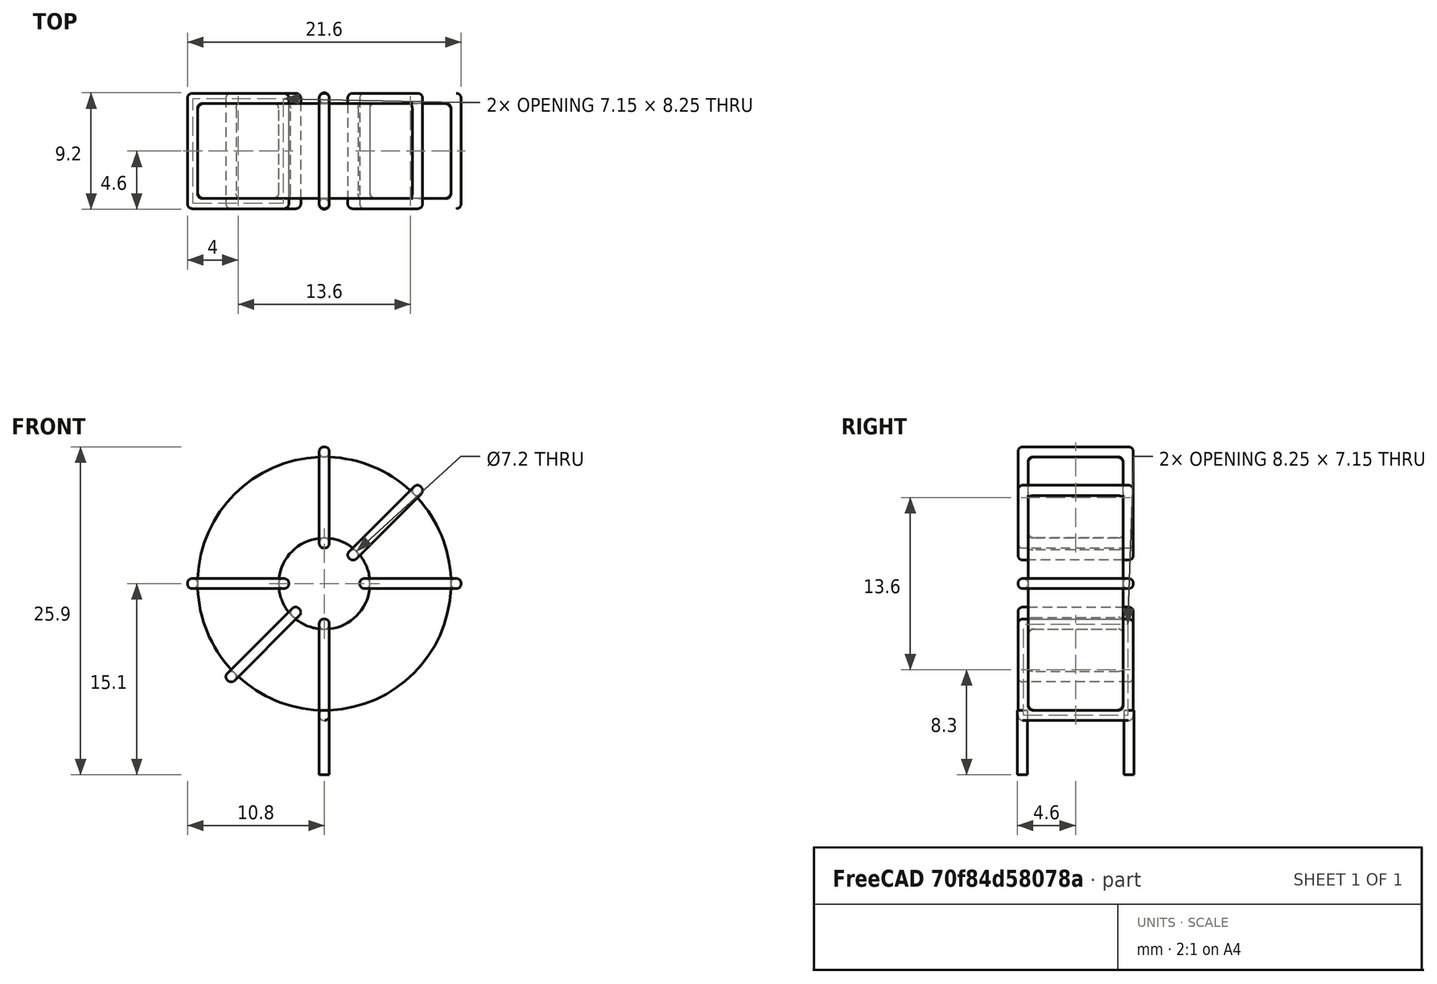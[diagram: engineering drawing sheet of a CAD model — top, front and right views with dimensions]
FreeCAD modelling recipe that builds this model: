
FCSTD DOCUMENT  (FreeCAD 0.16R6703 (Git))
Label: L_Toroid_Vertical_L21.6mm_W9.1mm_P8.40mm_Bourns_5700series
License: All rights reserved
LicenseURL: http://en.wikipedia.org/wiki/All_rights_reserved
objects: Sketcher::SketchObject×6, PartDesign::Pad×6, PartDesign::Fillet×5, Spreadsheet::Sheet×1
note: 23 computed .brp shape members not serialized (recipe doc carries the construction recipe); baked Part::Feature solids carry a one-line shape summary decoded from their .brp

FEATURE [Spreadsheet::Sheet] Spreadsheet  label="dimensions"
  cells = A1=Wx; B1(Wx)=21.6; C1(WW)=7.2; D1=21.6; A2=Wy; B2(Wy)=9.1; D2=9.1; A3=RM; B3(RMx)=8.4; C3(RMy)=0; A4=d_wire; B4(d_wire)=0.8; A5=H; B5(H)=21.6; A6=offsetx; B6(offsetx)=10.8
FEATURE [Sketcher::SketchObject] Sketch
  Placement = pos=(0,-4.2,0) rot=(1,0,0;1.5708rad)
  expr: Placement.Base.y = -Spreadsheet.RMx / 2
  expr: Constraints[0] = Spreadsheet.Wx / 2 - Spreadsheet.d_wire
  expr: Constraints[4] = Spreadsheet.WW / 2
  expr: Constraints[2] = Spreadsheet.Wx / 2 + Spreadsheet.d_wire + 0.5
  sketch-geometry (2):
    g0: Circle CenterX=0 CenterY=12.1 CenterZ=0 NormalX=0 NormalY=0 NormalZ=1 Radius=10
    g1: Circle CenterX=0 CenterY=12.1 CenterZ=0 NormalX=0 NormalY=0 NormalZ=1 Radius=3.6
  constraints (5):
    c: Radius(g0) = 10
    c: DistanceX(g-1,g0) = 0
    c: DistanceY(g-1,g0) = 12.1
    c: Coincident(g1,g0)
    c: Radius(g1) = 3.6
FEATURE [PartDesign::Pad] Pad
  Length = 7.5
  Length2 = 100
  Midplane = true
  Placement = pos=(0,-4.2,0) rot=(1,0,0;1.5708rad)
  Sketch = -> Sketch
  Type = 0
  expr: Length = Spreadsheet.Wy - 2 * Spreadsheet.d_wire
FEATURE [Sketcher::SketchObject] Sketch001
  Placement = pos=(0,0,1.3) rot=(0,0,1;0rad)
  expr: Placement.Base.z = 0.5 + Spreadsheet.d_wire
  expr: Constraints[4] = Spreadsheet.RMy
  expr: Constraints[2] = -Spreadsheet.RMx
  expr: Constraints[1] = Spreadsheet.d_wire / 2
  sketch-geometry (2):
    g0: Circle CenterX=0 CenterY=0 CenterZ=0 NormalX=0 NormalY=0 NormalZ=1 Radius=0.4
    g1: Circle CenterX=0 CenterY=-8.4 CenterZ=0 NormalX=0 NormalY=0 NormalZ=1 Radius=0.4
  constraints (5):
    c: Equal(g0,g1)
    c: Radius(g0) = 0.4
    c: DistanceY(g-1,g1) = -8.4
    c: Coincident(g0,g-1)
    c: DistanceX(g-1,g1) = 0
FEATURE [PartDesign::Pad] Pad001
  Length = 0.8
  Length2 = 4.3
  Placement = pos=(0,0,1.3) rot=(0,0,1;0rad)
  Reversed = true
  Sketch = -> Sketch001
  Type = 4
  expr: Length2 = 3.5 + Spreadsheet.d_wire
  expr: Length = Spreadsheet.d_wire
FEATURE [PartDesign::Fillet] Fillet
  Base = -> Pad [Edge6,Edge3,Edge2]
  Placement = pos=(0,-4.2,0) rot=(1,0,0;1.5708rad)
  Radius = 0.5
FEATURE [Sketcher::SketchObject] Sketch003
  Placement = pos=(0,0.35,12.1) rot=(1,0,0;3.14159rad)
  expr: Constraints[18] = Spreadsheet.d_wire
  expr: Constraints[16] = Spreadsheet.d_wire
  expr: Constraints[19] = Spreadsheet.d_wire
  expr: Constraints[17] = Spreadsheet.d_wire
  expr: Placement.Base.y = -1 * (Spreadsheet.RMx - Spreadsheet.Wy) / 2
  expr: Constraints[21] = (Spreadsheet.Wx - Spreadsheet.WW) / 2 - Spreadsheet.d_wire
  expr: Constraints[22] = Spreadsheet.Wx / 2 - Spreadsheet.d_wire
  expr: Constraints[43] = Spreadsheet.d_wire
  expr: Constraints[48] = Spreadsheet.Wx - Spreadsheet.d_wire * 2
  expr: Constraints[49] = Spreadsheet.Wy
  expr: Placement.Base.z = Spreadsheet.Wx / 2 + Spreadsheet.d_wire + 0.5
  sketch-geometry (16):
    g0: LineSegment StartX=-2.8 StartY=0 StartZ=0 EndX=-10.8 EndY=0 EndZ=0
    g1: LineSegment StartX=-10.8 StartY=0 StartZ=0 EndX=-10.8 EndY=9.1 EndZ=0
    g2: LineSegment StartX=-10.8 StartY=9.1 StartZ=0 EndX=-2.8 EndY=9.1 EndZ=0
    g3: LineSegment StartX=-2.8 StartY=9.1 StartZ=0 EndX=-2.8 EndY=0 EndZ=0
    g4: LineSegment StartX=-10 StartY=8.3 StartZ=0 EndX=-3.6 EndY=8.3 EndZ=0
    g5: LineSegment StartX=-3.6 StartY=8.3 StartZ=0 EndX=-3.6 EndY=0.8 EndZ=0
    g6: LineSegment StartX=-3.6 StartY=0.8 StartZ=0 EndX=-10 EndY=0.8 EndZ=0
    g7: LineSegment StartX=-10 StartY=0.8 StartZ=0 EndX=-10 EndY=8.3 EndZ=0
    g8: LineSegment StartX=2.8 StartY=9.1 StartZ=0 EndX=10.8 EndY=9.1 EndZ=0
    g9: LineSegment StartX=10.8 StartY=9.1 StartZ=0 EndX=10.8 EndY=0 EndZ=0
    g10: LineSegment StartX=10.8 StartY=0 StartZ=0 EndX=2.8 EndY=0 EndZ=0
    g11: LineSegment StartX=2.8 StartY=0 StartZ=0 EndX=2.8 EndY=9.1 EndZ=0
    g12: LineSegment StartX=3.6 StartY=8.3 StartZ=0 EndX=10 EndY=8.3 EndZ=0
    g13: LineSegment StartX=10 StartY=8.3 StartZ=0 EndX=10 EndY=0.8 EndZ=0
    g14: LineSegment StartX=10 StartY=0.8 StartZ=0 EndX=3.6 EndY=0.8 EndZ=0
    g15: LineSegment StartX=3.6 StartY=0.8 StartZ=0 EndX=3.6 EndY=8.3 EndZ=0
  constraints (50):
    c: Horizontal(g0)
    c: Coincident(g1,g0)
    c: Vertical(g1)
    c: Coincident(g2,g1)
    c: Horizontal(g2)
    c: Coincident(g3,g2)
    c: Coincident(g3,g0)
    c: Vertical(g3)
    c: Coincident(g4,g5)
    c: Coincident(g5,g6)
    c: Coincident(g6,g7)
    c: Coincident(g7,g4)
    c: Horizontal(g4)
    c: Horizontal(g6)
    c: Vertical(g5)
    c: Vertical(g7)
    c: DistanceX(g1,g4) = 0.8
    c: DistanceY(g4,g1) = 0.8
    c: DistanceX(g5,g0) = 0.8
    c: DistanceY(g0,g5) = 0.8
    c: DistanceY(g-1,g0) = 0
    c: DistanceX(g6,g6) = 6.4
    c: DistanceX(g6,g-1) = 10
    c: Coincident(g8,g9)
    c: Coincident(g9,g10)
    c: Coincident(g10,g11)
    c: Coincident(g11,g8)
    c: Horizontal(g8)
    c: Horizontal(g10)
    c: Vertical(g9)
    c: Vertical(g11)
    c: Coincident(g12,g13)
    c: Coincident(g13,g14)
    c: Coincident(g14,g15)
    c: Coincident(g15,g12)
    c: Horizontal(g12)
    c: Horizontal(g14)
    c: Vertical(g13)
    c: Vertical(g15)
    c: DistanceY(g8,g2) = 0
    c: DistanceY(g10,g0) = 0
    c: DistanceY(g14,g5) = 0
    c: DistanceY(g12,g4) = 0
    c: DistanceX(g8,g12) = 0.8
    c: Equal(g8,g2)
    c: Equal(g12,g4)
    c: Equal(g9,g1)
    c: Equal(g13,g7)
    c: DistanceX(g4,g12) = 20
    c: DistanceY(g0,g1) = 9.1
FEATURE [PartDesign::Pad] Pad002
  Length = 0.8
  Length2 = 100
  Midplane = true
  Placement = pos=(0,0.35,12.1) rot=(1,0,0;3.14159rad)
  Sketch = -> Sketch003
  Type = 0
  expr: Length = Spreadsheet.d_wire
FEATURE [PartDesign::Fillet] Fillet001
  Base = -> Pad002 [Edge38,Edge41,Edge42,Edge43,Edge29,Edge32,Edge33,Edge34,Edge25,Edge35,Edge36,Edge13,Edge14,Edge15,Edge16,Edge17,Edge18,Edge19,Edge1,Edge2,Edge3,Edge4,Edge5,Edge6,Edge7,Edge37,Edge39,Edge40,Edge20,Edge23,Edge24,Edge21,Edge22,Edge8,Edge9,Edge10,Edge11,Edge12,Edge26,Edge27,+8 more]
  Placement = pos=(0,0.35,12.1) rot=(1,0,0;3.14159rad)
  Radius = 0.376
  expr: Radius = Spreadsheet.d_wire * 0.47
FEATURE [Sketcher::SketchObject] Sketch004
  Placement = pos=(0,0.35,12.1) rot=(0.92388,0,0.382683;3.14159rad)
  expr: Constraints[18] = Spreadsheet.d_wire
  expr: Constraints[16] = Spreadsheet.d_wire
  expr: Constraints[19] = Spreadsheet.d_wire
  expr: Constraints[17] = Spreadsheet.d_wire
  expr: Placement.Base.y = -1 * (Spreadsheet.RMx - Spreadsheet.Wy) / 2
  expr: Constraints[21] = (Spreadsheet.Wx - Spreadsheet.WW) / 2 - Spreadsheet.d_wire
  expr: Constraints[22] = Spreadsheet.Wx / 2 - Spreadsheet.d_wire
  expr: Constraints[43] = Spreadsheet.d_wire
  expr: Constraints[48] = Spreadsheet.Wx - 2 * Spreadsheet.d_wire
  expr: Constraints[49] = Spreadsheet.Wy
  expr: Placement.Base.z = Spreadsheet.Wx / 2 + Spreadsheet.d_wire + 0.5
  sketch-geometry (16):
    g0: LineSegment StartX=-2.8 StartY=0 StartZ=0 EndX=-10.8 EndY=0 EndZ=0
    g1: LineSegment StartX=-10.8 StartY=0 StartZ=0 EndX=-10.8 EndY=9.1 EndZ=0
    g2: LineSegment StartX=-10.8 StartY=9.1 StartZ=0 EndX=-2.8 EndY=9.1 EndZ=0
    g3: LineSegment StartX=-2.8 StartY=9.1 StartZ=0 EndX=-2.8 EndY=0 EndZ=0
    g4: LineSegment StartX=-10 StartY=8.3 StartZ=0 EndX=-3.6 EndY=8.3 EndZ=0
    g5: LineSegment StartX=-3.6 StartY=8.3 StartZ=0 EndX=-3.6 EndY=0.8 EndZ=0
    g6: LineSegment StartX=-3.6 StartY=0.8 StartZ=0 EndX=-10 EndY=0.8 EndZ=0
    g7: LineSegment StartX=-10 StartY=0.8 StartZ=0 EndX=-10 EndY=8.3 EndZ=0
    g8: LineSegment StartX=2.8 StartY=9.1 StartZ=0 EndX=10.8 EndY=9.1 EndZ=0
    g9: LineSegment StartX=10.8 StartY=9.1 StartZ=0 EndX=10.8 EndY=0 EndZ=0
    g10: LineSegment StartX=10.8 StartY=0 StartZ=0 EndX=2.8 EndY=0 EndZ=0
    g11: LineSegment StartX=2.8 StartY=0 StartZ=0 EndX=2.8 EndY=9.1 EndZ=0
    g12: LineSegment StartX=3.6 StartY=8.3 StartZ=0 EndX=10 EndY=8.3 EndZ=0
    g13: LineSegment StartX=10 StartY=8.3 StartZ=0 EndX=10 EndY=0.8 EndZ=0
    g14: LineSegment StartX=10 StartY=0.8 StartZ=0 EndX=3.6 EndY=0.8 EndZ=0
    g15: LineSegment StartX=3.6 StartY=0.8 StartZ=0 EndX=3.6 EndY=8.3 EndZ=0
  constraints (50):
    c: Horizontal(g0)
    c: Coincident(g1,g0)
    c: Vertical(g1)
    c: Coincident(g2,g1)
    c: Horizontal(g2)
    c: Coincident(g3,g2)
    c: Coincident(g3,g0)
    c: Vertical(g3)
    c: Coincident(g4,g5)
    c: Coincident(g5,g6)
    c: Coincident(g6,g7)
    c: Coincident(g7,g4)
    c: Horizontal(g4)
    c: Horizontal(g6)
    c: Vertical(g5)
    c: Vertical(g7)
    c: DistanceX(g1,g4) = 0.8
    c: DistanceY(g4,g1) = 0.8
    c: DistanceX(g5,g0) = 0.8
    c: DistanceY(g0,g5) = 0.8
    c: DistanceY(g-1,g0) = 0
    c: DistanceX(g6,g6) = 6.4
    c: DistanceX(g6,g-1) = 10
    c: Coincident(g8,g9)
    c: Coincident(g9,g10)
    c: Coincident(g10,g11)
    c: Coincident(g11,g8)
    c: Horizontal(g8)
    c: Horizontal(g10)
    c: Vertical(g9)
    c: Vertical(g11)
    c: Coincident(g12,g13)
    c: Coincident(g13,g14)
    c: Coincident(g14,g15)
    c: Coincident(g15,g12)
    c: Horizontal(g12)
    c: Horizontal(g14)
    c: Vertical(g13)
    c: Vertical(g15)
    c: DistanceY(g8,g2) = 0
    c: DistanceY(g10,g0) = 0
    c: DistanceY(g14,g5) = 0
    c: DistanceY(g12,g4) = 0
    c: DistanceX(g8,g12) = 0.8
    c: Equal(g8,g2)
    c: Equal(g12,g4)
    c: Equal(g9,g1)
    c: Equal(g13,g7)
    c: DistanceX(g4,g12) = 20
    c: DistanceY(g0,g1) = 9.1
FEATURE [PartDesign::Pad] Pad003
  Length = 0.8
  Length2 = 100
  Midplane = true
  Placement = pos=(0,0.35,12.1) rot=(0.92388,0,0.382683;3.14159rad)
  Sketch = -> Sketch004
  Type = 0
  expr: Length = Spreadsheet.d_wire
FEATURE [PartDesign::Fillet] Fillet002
  Base = -> Pad003 [Edge38,Edge41,Edge42,Edge43,Edge29,Edge32,Edge33,Edge34,Edge25,Edge35,Edge36,Edge13,Edge14,Edge15,Edge16,Edge17,Edge18,Edge19,Edge1,Edge2,Edge3,Edge4,Edge5,Edge6,Edge7,Edge37,Edge39,Edge40,Edge20,Edge23,Edge24,Edge21,Edge22,Edge8,Edge9,Edge10,Edge11,Edge12,Edge26,Edge27,+8 more]
  Placement = pos=(0,0.35,12.1) rot=(0.92388,0,0.382683;3.14159rad)
  Radius = 0.376
  expr: Radius = Spreadsheet.d_wire * 0.47
FEATURE [Sketcher::SketchObject] Sketch005
  Placement = pos=(0,0.35,12.1) rot=(0.92388,0,-0.382683;3.14159rad)
  expr: Constraints[18] = Spreadsheet.d_wire
  expr: Constraints[16] = Spreadsheet.d_wire
  expr: Constraints[19] = Spreadsheet.d_wire
  expr: Constraints[17] = Spreadsheet.d_wire
  expr: Placement.Base.y = -1 * (Spreadsheet.RMx - Spreadsheet.Wy) / 2
  expr: Constraints[21] = (Spreadsheet.Wx - Spreadsheet.WW) / 2 - Spreadsheet.d_wire
  expr: Constraints[22] = Spreadsheet.Wx / 2 - Spreadsheet.d_wire
  expr: Constraints[43] = Spreadsheet.d_wire
  expr: Constraints[48] = Spreadsheet.Wx - 2 * Spreadsheet.d_wire
  expr: Constraints[49] = Spreadsheet.Wy
  expr: Placement.Base.z = Spreadsheet.Wx / 2 + Spreadsheet.d_wire + 0.5
  sketch-geometry (16):
    g0: LineSegment StartX=-2.8 StartY=0 StartZ=0 EndX=-10.8 EndY=0 EndZ=0
    g1: LineSegment StartX=-10.8 StartY=0 StartZ=0 EndX=-10.8 EndY=9.1 EndZ=0
    g2: LineSegment StartX=-10.8 StartY=9.1 StartZ=0 EndX=-2.8 EndY=9.1 EndZ=0
    g3: LineSegment StartX=-2.8 StartY=9.1 StartZ=0 EndX=-2.8 EndY=0 EndZ=0
    g4: LineSegment StartX=-10 StartY=8.3 StartZ=0 EndX=-3.6 EndY=8.3 EndZ=0
    g5: LineSegment StartX=-3.6 StartY=8.3 StartZ=0 EndX=-3.6 EndY=0.8 EndZ=0
    g6: LineSegment StartX=-3.6 StartY=0.8 StartZ=0 EndX=-10 EndY=0.8 EndZ=0
    g7: LineSegment StartX=-10 StartY=0.8 StartZ=0 EndX=-10 EndY=8.3 EndZ=0
    g8: LineSegment StartX=2.8 StartY=9.1 StartZ=0 EndX=10.8 EndY=9.1 EndZ=0
    g9: LineSegment StartX=10.8 StartY=9.1 StartZ=0 EndX=10.8 EndY=0 EndZ=0
    g10: LineSegment StartX=10.8 StartY=0 StartZ=0 EndX=2.8 EndY=0 EndZ=0
    g11: LineSegment StartX=2.8 StartY=0 StartZ=0 EndX=2.8 EndY=9.1 EndZ=0
    g12: LineSegment StartX=3.6 StartY=8.3 StartZ=0 EndX=10 EndY=8.3 EndZ=0
    g13: LineSegment StartX=10 StartY=8.3 StartZ=0 EndX=10 EndY=0.8 EndZ=0
    g14: LineSegment StartX=10 StartY=0.8 StartZ=0 EndX=3.6 EndY=0.8 EndZ=0
    g15: LineSegment StartX=3.6 StartY=0.8 StartZ=0 EndX=3.6 EndY=8.3 EndZ=0
  constraints (50):
    c: Horizontal(g0)
    c: Coincident(g1,g0)
    c: Vertical(g1)
    c: Coincident(g2,g1)
    c: Horizontal(g2)
    c: Coincident(g3,g2)
    c: Coincident(g3,g0)
    c: Vertical(g3)
    c: Coincident(g4,g5)
    c: Coincident(g5,g6)
    c: Coincident(g6,g7)
    c: Coincident(g7,g4)
    c: Horizontal(g4)
    c: Horizontal(g6)
    c: Vertical(g5)
    c: Vertical(g7)
    c: DistanceX(g1,g4) = 0.8
    c: DistanceY(g4,g1) = 0.8
    c: DistanceX(g5,g0) = 0.8
    c: DistanceY(g0,g5) = 0.8
    c: DistanceY(g-1,g0) = 0
    c: DistanceX(g6,g6) = 6.4
    c: DistanceX(g6,g-1) = 10
    c: Coincident(g8,g9)
    c: Coincident(g9,g10)
    c: Coincident(g10,g11)
    c: Coincident(g11,g8)
    c: Horizontal(g8)
    c: Horizontal(g10)
    c: Vertical(g9)
    c: Vertical(g11)
    c: Coincident(g12,g13)
    c: Coincident(g13,g14)
    c: Coincident(g14,g15)
    c: Coincident(g15,g12)
    c: Horizontal(g12)
    c: Horizontal(g14)
    c: Vertical(g13)
    c: Vertical(g15)
    c: DistanceY(g8,g2) = 0
    c: DistanceY(g10,g0) = 0
    c: DistanceY(g14,g5) = 0
    c: DistanceY(g12,g4) = 0
    c: DistanceX(g8,g12) = 0.8
    c: Equal(g8,g2)
    c: Equal(g12,g4)
    c: Equal(g9,g1)
    c: Equal(g13,g7)
    c: DistanceX(g4,g12) = 20
    c: DistanceY(g0,g1) = 9.1
FEATURE [PartDesign::Pad] Pad004
  Length = 0.8
  Length2 = 100
  Midplane = true
  Placement = pos=(0,0.35,12.1) rot=(0.92388,0,-0.382683;3.14159rad)
  Sketch = -> Sketch005
  Type = 0
  expr: Length = Spreadsheet.d_wire
FEATURE [PartDesign::Fillet] Fillet003
  Base = -> Pad004 [Edge38,Edge41,Edge42,Edge43,Edge29,Edge32,Edge33,Edge34,Edge25,Edge35,Edge36,Edge13,Edge14,Edge15,Edge16,Edge17,Edge18,Edge19,Edge1,Edge2,Edge3,Edge4,Edge5,Edge6,Edge7,Edge37,Edge39,Edge40,Edge20,Edge23,Edge24,Edge21,Edge22,Edge8,Edge9,Edge10,Edge11,Edge12,Edge26,Edge27,+8 more]
  Placement = pos=(0,0.35,12.1) rot=(0.92388,0,-0.382683;3.14159rad)
  Radius = 0.376
  expr: Radius = Spreadsheet.d_wire * 0.47
FEATURE [Sketcher::SketchObject] Sketch006
  Placement = pos=(0,0.35,12.1) rot=(0.707107,0,0.707107;3.14159rad)
  expr: Constraints[18] = Spreadsheet.d_wire
  expr: Constraints[16] = Spreadsheet.d_wire
  expr: Constraints[19] = Spreadsheet.d_wire
  expr: Constraints[17] = Spreadsheet.d_wire
  expr: Placement.Base.y = -1 * (Spreadsheet.RMx - Spreadsheet.Wy) / 2
  expr: Constraints[21] = (Spreadsheet.Wx - Spreadsheet.WW) / 2 - Spreadsheet.d_wire
  expr: Constraints[22] = Spreadsheet.Wx / 2 - Spreadsheet.d_wire
  expr: Constraints[43] = Spreadsheet.d_wire
  expr: Constraints[48] = Spreadsheet.Wx - Spreadsheet.d_wire * 2
  expr: Constraints[49] = Spreadsheet.Wy
  expr: Placement.Base.z = Spreadsheet.Wx / 2 + Spreadsheet.d_wire + 0.5
  sketch-geometry (16):
    g0: LineSegment StartX=-2.8 StartY=0 StartZ=0 EndX=-10.8 EndY=0 EndZ=0
    g1: LineSegment StartX=-10.8 StartY=0 StartZ=0 EndX=-10.8 EndY=9.1 EndZ=0
    g2: LineSegment StartX=-10.8 StartY=9.1 StartZ=0 EndX=-2.8 EndY=9.1 EndZ=0
    g3: LineSegment StartX=-2.8 StartY=9.1 StartZ=0 EndX=-2.8 EndY=0 EndZ=0
    g4: LineSegment StartX=-10 StartY=8.3 StartZ=0 EndX=-3.6 EndY=8.3 EndZ=0
    g5: LineSegment StartX=-3.6 StartY=8.3 StartZ=0 EndX=-3.6 EndY=0.8 EndZ=0
    g6: LineSegment StartX=-3.6 StartY=0.8 StartZ=0 EndX=-10 EndY=0.8 EndZ=0
    g7: LineSegment StartX=-10 StartY=0.8 StartZ=0 EndX=-10 EndY=8.3 EndZ=0
    g8: LineSegment StartX=2.8 StartY=9.1 StartZ=0 EndX=10.8 EndY=9.1 EndZ=0
    g9: LineSegment StartX=10.8 StartY=9.1 StartZ=0 EndX=10.8 EndY=0 EndZ=0
    g10: LineSegment StartX=10.8 StartY=0 StartZ=0 EndX=2.8 EndY=0 EndZ=0
    g11: LineSegment StartX=2.8 StartY=0 StartZ=0 EndX=2.8 EndY=9.1 EndZ=0
    g12: LineSegment StartX=3.6 StartY=8.3 StartZ=0 EndX=10 EndY=8.3 EndZ=0
    g13: LineSegment StartX=10 StartY=8.3 StartZ=0 EndX=10 EndY=0.8 EndZ=0
    g14: LineSegment StartX=10 StartY=0.8 StartZ=0 EndX=3.6 EndY=0.8 EndZ=0
    g15: LineSegment StartX=3.6 StartY=0.8 StartZ=0 EndX=3.6 EndY=8.3 EndZ=0
  constraints (50):
    c: Horizontal(g0)
    c: Coincident(g1,g0)
    c: Vertical(g1)
    c: Coincident(g2,g1)
    c: Horizontal(g2)
    c: Coincident(g3,g2)
    c: Coincident(g3,g0)
    c: Vertical(g3)
    c: Coincident(g4,g5)
    c: Coincident(g5,g6)
    c: Coincident(g6,g7)
    c: Coincident(g7,g4)
    c: Horizontal(g4)
    c: Horizontal(g6)
    c: Vertical(g5)
    c: Vertical(g7)
    c: DistanceX(g1,g4) = 0.8
    c: DistanceY(g4,g1) = 0.8
    c: DistanceX(g5,g0) = 0.8
    c: DistanceY(g0,g5) = 0.8
    c: DistanceY(g-1,g0) = 0
    c: DistanceX(g6,g6) = 6.4
    c: DistanceX(g6,g-1) = 10
    c: Coincident(g8,g9)
    c: Coincident(g9,g10)
    c: Coincident(g10,g11)
    c: Coincident(g11,g8)
    c: Horizontal(g8)
    c: Horizontal(g10)
    c: Vertical(g9)
    c: Vertical(g11)
    c: Coincident(g12,g13)
    c: Coincident(g13,g14)
    c: Coincident(g14,g15)
    c: Coincident(g15,g12)
    c: Horizontal(g12)
    c: Horizontal(g14)
    c: Vertical(g13)
    c: Vertical(g15)
    c: DistanceY(g8,g2) = 0
    c: DistanceY(g10,g0) = 0
    c: DistanceY(g14,g5) = 0
    c: DistanceY(g12,g4) = 0
    c: DistanceX(g8,g12) = 0.8
    c: Equal(g8,g2)
    c: Equal(g12,g4)
    c: Equal(g9,g1)
    c: Equal(g13,g7)
    c: DistanceX(g4,g12) = 20
    c: DistanceY(g0,g1) = 9.1
FEATURE [PartDesign::Pad] Pad005
  Length = 0.8
  Length2 = 100
  Midplane = true
  Placement = pos=(0,0.35,12.1) rot=(0.707107,0,0.707107;3.14159rad)
  Sketch = -> Sketch006
  Type = 0
  expr: Length = Spreadsheet.d_wire
FEATURE [PartDesign::Fillet] Fillet004
  Base = -> Pad005 [Edge38,Edge41,Edge42,Edge43,Edge29,Edge32,Edge33,Edge34,Edge25,Edge35,Edge36,Edge13,Edge14,Edge15,Edge16,Edge17,Edge18,Edge19,Edge1,Edge2,Edge3,Edge4,Edge5,Edge6,Edge7,Edge37,Edge39,Edge40,Edge20,Edge23,Edge24,Edge21,Edge22,Edge8,Edge9,Edge10,Edge11,Edge12,Edge26,Edge27,+8 more]
  Placement = pos=(0,0.35,12.1) rot=(0.707107,0,0.707107;3.14159rad)
  Radius = 0.376
  expr: Radius = Spreadsheet.d_wire * 0.47
